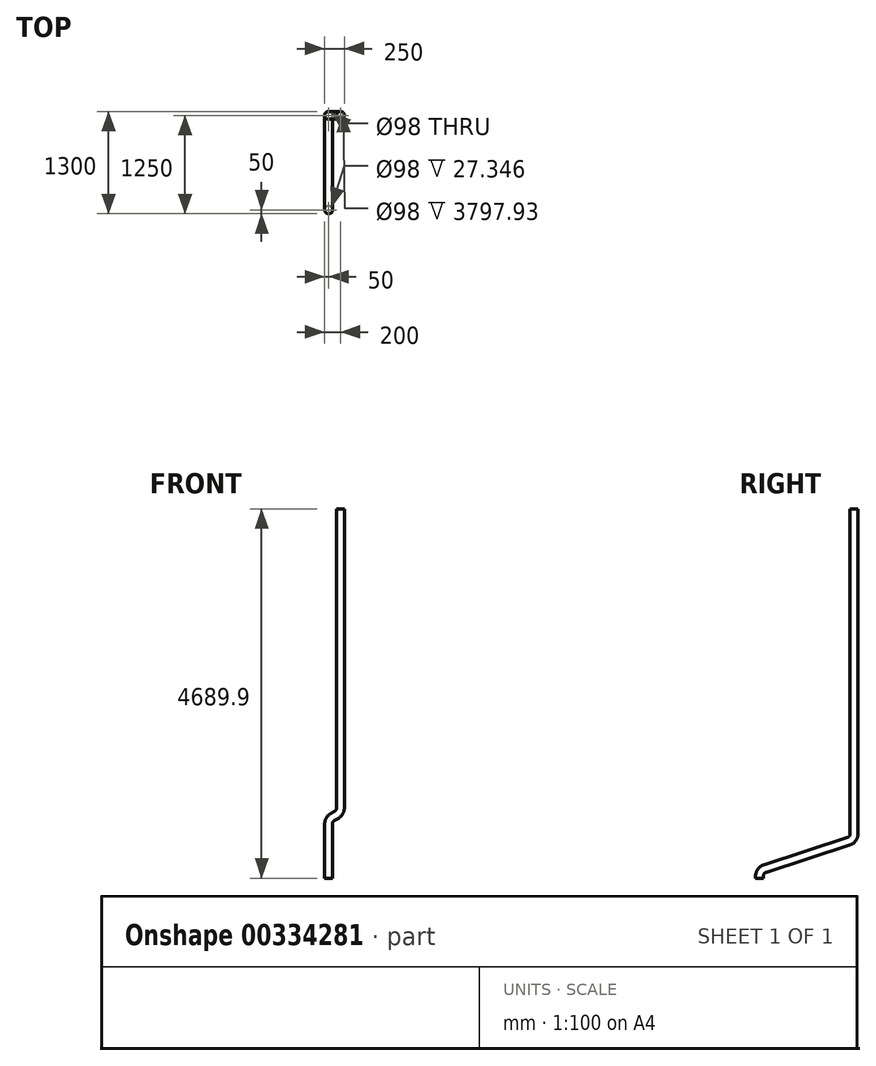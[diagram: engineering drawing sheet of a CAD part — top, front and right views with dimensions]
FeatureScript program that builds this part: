
annotation { "Feature Type Name" : "Feature", "Feature Type Description" : "" }
export const myFeature = defineFeature(function(context is Context, id is Id, definition is map)
    precondition{}
    {
        {
            var Q0;
            Q0=qCreatedBy(makeId("Right.planeOp"),FACE);
            var sketch = newSketch(context, id + "F0", { "sketchPlane" : qUnion([Q0])});
            skLineSegment(sketch, "E0", {"start": v(0, 0) * mm, "end": v(0, -27.35) * mm});
            skLineSegment(sketch, "E1", {"start": v(-69.1, -122.45) * mm, "end": v(-1130.9, -467.45) * mm});
            skLineSegment(sketch, "E2", {"start": v(-1200, -562.56) * mm, "end": v(-1200, -589.9) * mm});
            skPoint(sketch, "E3.visualSharp", {"position": v(0, -100) * mm});
            skArc(sketch, "E3.filletArc", {"start": v(-69.1, -122.45) * mm, "mid": v(-19.1, -86.12) * mm, "end": v(0, -27.35) * mm});
            skPoint(sketch, "E4.visualSharp", {"position": v(-1200, -489.9) * mm});
            skArc(sketch, "E4.filletArc", {"start": v(-1130.9, -467.45) * mm, "mid": v(-1180.9, -503.78) * mm, "end": v(-1200, -562.56) * mm});
            skSolve(sketch);
        }
        {
            var Q0;
            Q0=qCreatedBy(makeId("Top.planeOp"),FACE);
            var sketch = newSketch(context, id + "F1", { "sketchPlane" : qUnion([Q0])});
            skCircle(sketch, "E5", {"center": v(0, 0) * mm, "radius": 50 * mm});
            skCircle(sketch, "E6", {"center": v(0, 0) * mm, "radius": 49 * mm});
            skSolve(sketch);
        }
        {
            var Q0;
            Q0=makeQuery(id+"F1.imprint","IMPRINT",FACE,{"disambiguationData":[TD([[makeQuery(id+"F1.imprint","IMPRINT",EDGE,{"derivedFrom":sQuery(id+"F1.wireOp",EDGE,"E5")}),1.0]])]});
            var Q1;
            Q1=sQuery(id+"F0.wireOp",EDGE,"E0");
            var Q2;
            Q2=sQuery(id+"F0.wireOp",EDGE,"E3.filletArc");
            var Q3;
            Q3=sQuery(id+"F0.wireOp",EDGE,"E1");
            var Q4;
            Q4=sQuery(id+"F0.wireOp",EDGE,"E4.filletArc");
            var Q5;
            Q5=sQuery(id+"F0.wireOp",EDGE,"E2");
            sweep(context, id + "F2", {"profiles" : qUnion([Q0]), "path" : qUnion([Q1, Q2, Q3, Q4, Q5])});
        }
        {
            var Q0;
            Q0=qCreatedBy(makeId("Front.planeOp"),FACE);
            var sketch = newSketch(context, id + "F3", { "sketchPlane" : qUnion([Q0])});
            skLineSegment(sketch, "E7", {"start": v(0, 0) * mm, "end": v(0, 100) * mm});
            skLineSegment(sketch, "E8", {"start": v(-50, 186.6) * mm, "end": v(-100, 215.47) * mm});
            skLineSegment(sketch, "E9", {"start": v(-150, 302.07) * mm, "end": v(-150, 4100) * mm});
            skPoint(sketch, "E10.visualSharp", {"position": v(0, 157.74) * mm});
            skArc(sketch, "E10.filletArc", {"start": v(0, 100) * mm, "mid": v(-13.4, 150) * mm, "end": v(-50, 186.6) * mm});
            skPoint(sketch, "E11.visualSharp", {"position": v(-150, 244.34) * mm});
            skArc(sketch, "E11.filletArc", {"start": v(-150, 302.07) * mm, "mid": v(-136.6, 252.07) * mm, "end": v(-100, 215.47) * mm});
            skSolve(sketch);
        }
        {
            var Q0;
            Q0=makeQuery(id+"F2.opSweep","CAP_FACE",FACE,{"disambiguationData":[OSD([sQuery(id+"F0.wireOp",VERTEX,"E0.start"),sQuery(id+"F1.wireOp",EDGE,"E5"),sQuery(id+"F1.wireOp",EDGE,"E6")])],"isStart":true});
            var Q1;
            Q1=sQuery(id+"F3.wireOp",EDGE,"E7");
            var Q2;
            Q2=sQuery(id+"F3.wireOp",EDGE,"E10.filletArc");
            var Q3;
            Q3=sQuery(id+"F3.wireOp",EDGE,"E8");
            var Q4;
            Q4=sQuery(id+"F3.wireOp",EDGE,"E11.filletArc");
            var Q5;
            Q5=sQuery(id+"F3.wireOp",EDGE,"E9");
            sweep(context, id + "F4", {"operationType" : NewBodyOperationType.ADD, "profiles" : qUnion([Q0]), "path" : qUnion([Q1, Q2, Q3, Q4, Q5])});
        }
        {
            var Q0;
            Q0=qCreatedBy(makeId("Right.planeOp"),FACE);
            cPlane(context, id + "F5", {"entities" : qUnion([Q0]), "cplaneType" : CPlaneType.OFFSET, "offset" : 200 * mm, "width" : 150 * mm, "height" : 150 * mm});
        }
        {
            var Q0;
            Q0=makeQuery(id+"F2.opSweep","SWEPT_BODY",BODY,{"disambiguationData":[OSD([sQuery(id+"F0.wireOp",EDGE,"E2"),sQuery(id+"F1.wireOp",EDGE,"E5"),sQuery(id+"F1.wireOp",EDGE,"E6")])]});
            var Q1;
            Q1=qCreatedBy(id+"F5.planeOp",FACE);
            mirror(context, id + "F6", {"entities" : qUnion([Q0]), "mirrorPlane" : qUnion([Q1])});
        }
        {
            var Q0;
            Q0=makeQuery(id+"F2.opSweep","SWEPT_BODY",BODY,{"disambiguationData":[OSD([sQuery(id+"F0.wireOp",EDGE,"E2"),sQuery(id+"F1.wireOp",EDGE,"E5"),sQuery(id+"F1.wireOp",EDGE,"E6")])]});
            deleteBodies(context, id + "F7", {"entities" : qUnion([Q0])});
        }
    });
